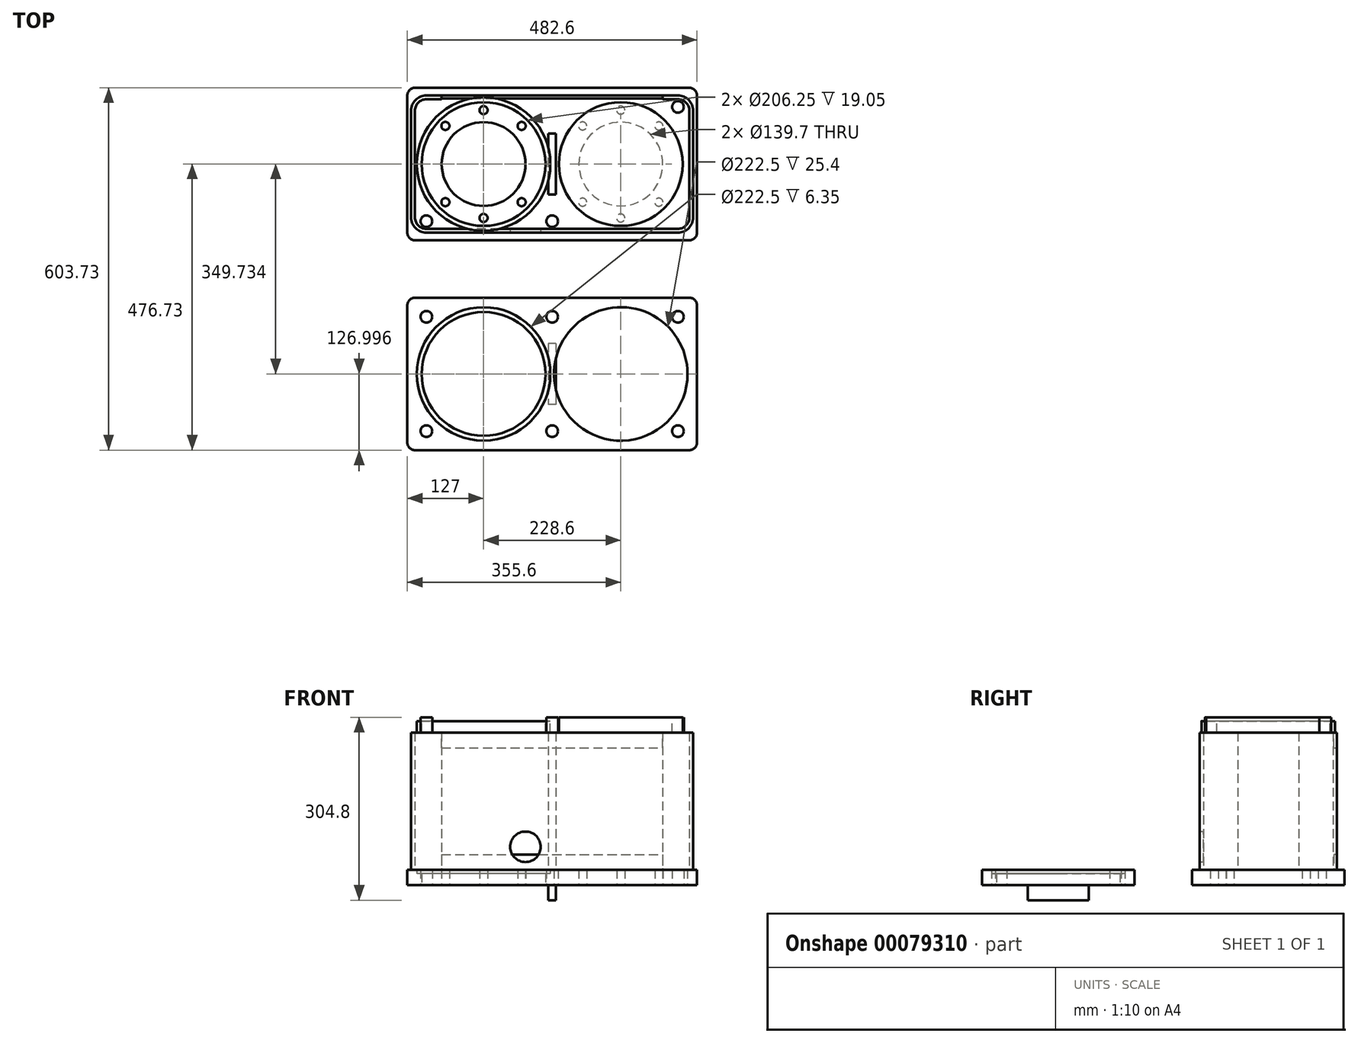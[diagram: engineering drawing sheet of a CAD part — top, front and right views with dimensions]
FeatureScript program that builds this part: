
annotation { "Feature Type Name" : "Feature", "Feature Type Description" : "" }
export const myFeature = defineFeature(function(context is Context, id is Id, definition is map)
    precondition{}
    {
        {
            var Q0;
            Q0=qCreatedBy(makeId("Top.planeOp"),FACE);
            var sketch = newSketch(context, id + "F0", { "sketchPlane" : qUnion([Q0])});
            skLineSegment(sketch, "E0.bottom", {"start": v(241.3, -127) * mm, "end": v(-241.3, -127) * mm});
            skLineSegment(sketch, "E0.top", {"start": v(241.3, 127) * mm, "end": v(-241.3, 127) * mm});
            skLineSegment(sketch, "E0.left", {"start": v(241.3, -127) * mm, "end": v(241.3, 127) * mm});
            skLineSegment(sketch, "E0.right", {"start": v(-241.3, -127) * mm, "end": v(-241.3, 127) * mm});
            skPoint(sketch, "E0.middle", {"position": v(0, 0) * mm});
            skSolve(sketch);
        }
        {
            var Q0;
            Q0=makeQuery(id+"F0.imprint","IMPRINT",FACE,{"disambiguationData":[TD([[makeQuery(id+"F0.imprint","IMPRINT",EDGE,{"derivedFrom":sQuery(id+"F0.wireOp",EDGE,"E0.bottom")}),-1.0]])]});
            extrude(context, id + "F1", {"entities" : qUnion([Q0]), "depth" : 25.4 * mm});
        }
        {
            var Q0;
            Q0=makeQuery(id+"F1.opExtrude","CAP_FACE",FACE,{"disambiguationData":[OSD([sQuery(id+"F0.wireOp",EDGE,"E0.bottom"),sQuery(id+"F0.wireOp",EDGE,"E0.top"),sQuery(id+"F0.wireOp",EDGE,"E0.left"),sQuery(id+"F0.wireOp",EDGE,"E0.right")])],"isStart":false});
            var sketch = newSketch(context, id + "F2", { "sketchPlane" : qUnion([Q0])});
            skLineSegment(sketch, "E1.bottom", {"start": v(209.55, -114.3) * mm, "end": v(-209.55, -114.3) * mm});
            skLineSegment(sketch, "E1.left", {"start": v(234.95, -88.9) * mm, "end": v(234.95, 88.9) * mm});
            skLineSegment(sketch, "E1.right", {"start": v(-234.95, -88.9) * mm, "end": v(-234.95, 88.9) * mm});
            skPoint(sketch, "E1.middle", {"position": v(0, 0) * mm});
            skLineSegment(sketch, "E2.bottom", {"start": v(209.55, -107.95) * mm, "end": v(-209.55, -107.95) * mm});
            skLineSegment(sketch, "E2.left", {"start": v(228.6, -88.9) * mm, "end": v(228.6, 88.9) * mm});
            skLineSegment(sketch, "E2.right", {"start": v(-228.6, -88.9) * mm, "end": v(-228.6, 88.9) * mm});
            skLineSegment(sketch, "E3", {"start": v(-209.55, 114.3) * mm, "end": v(-184.15, 114.3) * mm});
            skLineSegment(sketch, "E4", {"start": v(-209.55, 107.95) * mm, "end": v(-184.14, 107.95) * mm});
            skLineSegment(sketch, "E5", {"start": v(-184.15, 114.3) * mm, "end": v(-184.14, 107.95) * mm});
            skLineSegment(sketch, "E6", {"start": v(209.55, 114.3) * mm, "end": v(184.15, 114.3) * mm});
            skLineSegment(sketch, "E7", {"start": v(184.15, 114.3) * mm, "end": v(184.15, 107.95) * mm});
            skLineSegment(sketch, "E8", {"start": v(184.15, 107.95) * mm, "end": v(209.55, 107.95) * mm});
            skPoint(sketch, "E9.visualSharp", {"position": v(-234.95, 114.3) * mm});
            skArc(sketch, "E9.filletArc", {"start": v(-209.55, 114.3) * mm, "mid": v(-227.51, 106.86) * mm, "end": v(-234.95, 88.9) * mm});
            skPoint(sketch, "E10.visualSharp", {"position": v(-234.95, -114.3) * mm});
            skArc(sketch, "E10.filletArc", {"start": v(-234.95, -88.9) * mm, "mid": v(-227.51, -106.86) * mm, "end": v(-209.55, -114.3) * mm});
            skPoint(sketch, "E11.visualSharp", {"position": v(234.95, -114.3) * mm});
            skArc(sketch, "E11.filletArc", {"start": v(209.55, -114.3) * mm, "mid": v(227.51, -106.86) * mm, "end": v(234.95, -88.9) * mm});
            skPoint(sketch, "E12.visualSharp", {"position": v(234.95, 114.3) * mm});
            skArc(sketch, "E12.filletArc", {"start": v(234.95, 88.9) * mm, "mid": v(227.51, 106.86) * mm, "end": v(209.55, 114.3) * mm});
            skPoint(sketch, "E13.visualSharp", {"position": v(-228.6, 107.95) * mm});
            skArc(sketch, "E13.filletArc", {"start": v(-209.55, 107.95) * mm, "mid": v(-223.02, 102.37) * mm, "end": v(-228.6, 88.9) * mm});
            skPoint(sketch, "E14.visualSharp", {"position": v(-228.6, -107.95) * mm});
            skArc(sketch, "E14.filletArc", {"start": v(-228.6, -88.9) * mm, "mid": v(-223.02, -102.37) * mm, "end": v(-209.55, -107.95) * mm});
            skPoint(sketch, "E15.visualSharp", {"position": v(228.6, -107.95) * mm});
            skArc(sketch, "E15.filletArc", {"start": v(209.55, -107.95) * mm, "mid": v(223.02, -102.37) * mm, "end": v(228.6, -88.9) * mm});
            skPoint(sketch, "E16.visualSharp", {"position": v(228.6, 107.95) * mm});
            skArc(sketch, "E16.filletArc", {"start": v(228.6, 88.9) * mm, "mid": v(223.02, 102.37) * mm, "end": v(209.55, 107.95) * mm});
            skLineSegment(sketch, "E17.bottom", {"start": v(6.35, -50.8) * mm, "end": v(-6.35, -50.8) * mm});
            skLineSegment(sketch, "E17.top", {"start": v(6.35, 50.8) * mm, "end": v(-6.35, 50.8) * mm});
            skLineSegment(sketch, "E17.left", {"start": v(6.35, -50.8) * mm, "end": v(6.35, 50.8) * mm});
            skLineSegment(sketch, "E17.right", {"start": v(-6.35, -50.8) * mm, "end": v(-6.35, 50.8) * mm});
            skSolve(sketch);
        }
        {
            var Q0;
            Q0=makeQuery(id+"F2.imprint","IMPRINT",FACE,{"disambiguationData":[TD([[makeQuery(id+"F2.imprint","IMPRINT",EDGE,{"derivedFrom":sQuery(id+"F2.wireOp",EDGE,"E1.bottom")}),-1.0]])]});
            var Q1;
            Q1=makeQuery(id+"F2.imprint","IMPRINT",FACE,{"disambiguationData":[TD([[makeQuery(id+"F2.imprint","IMPRINT",EDGE,{"derivedFrom":sQuery(id+"F2.wireOp",EDGE,"E17.bottom")}),-1.0]])]});
            extrude(context, id + "F3", {"entities" : qUnion([Q0, Q1]), "operationType" : NewBodyOperationType.ADD, "depth" : 228.6 * mm});
        }
        {
            var Q0;
            Q0=makeQuery(id+"F3.opExtrude","CAP_FACE",FACE,{"disambiguationData":[OSD([sQuery(id+"F2.wireOp",EDGE,"E1.bottom"),sQuery(id+"F2.wireOp",EDGE,"E1.left"),sQuery(id+"F2.wireOp",EDGE,"E1.right"),sQuery(id+"F2.wireOp",EDGE,"E2.bottom"),sQuery(id+"F2.wireOp",EDGE,"E2.left"),sQuery(id+"F2.wireOp",EDGE,"E2.right"),sQuery(id+"F2.wireOp",EDGE,"E3"),sQuery(id+"F2.wireOp",EDGE,"E4"),sQuery(id+"F2.wireOp",EDGE,"E5"),sQuery(id+"F2.wireOp",EDGE,"E6"),sQuery(id+"F2.wireOp",EDGE,"E7"),sQuery(id+"F2.wireOp",EDGE,"E8"),sQuery(id+"F2.wireOp",EDGE,"E9.filletArc"),sQuery(id+"F2.wireOp",EDGE,"E10.filletArc"),sQuery(id+"F2.wireOp",EDGE,"E11.filletArc"),sQuery(id+"F2.wireOp",EDGE,"E12.filletArc"),sQuery(id+"F2.wireOp",EDGE,"E13.filletArc"),sQuery(id+"F2.wireOp",EDGE,"E14.filletArc"),sQuery(id+"F2.wireOp",EDGE,"E15.filletArc"),sQuery(id+"F2.wireOp",EDGE,"E16.filletArc")])],"isStart":false});
            var sketch = newSketch(context, id + "F4", { "sketchPlane" : qUnion([Q0])});
            skLineSegment(sketch, "E18.bottom", {"start": v(241.3, -127) * mm, "end": v(-241.3, -127) * mm});
            skLineSegment(sketch, "E18.top", {"start": v(241.3, 127) * mm, "end": v(-241.3, 127) * mm});
            skLineSegment(sketch, "E18.left", {"start": v(241.3, -127) * mm, "end": v(241.3, 127) * mm});
            skLineSegment(sketch, "E18.right", {"start": v(-241.3, -127) * mm, "end": v(-241.3, 127) * mm});
            skPoint(sketch, "E18.middle", {"position": v(0, 0) * mm});
            skSolve(sketch);
        }
        {
            var Q0;
            Q0 = qSketchRegion(id + "F4", true);
            extrude(context, id + "F5", {"entities" : qUnion([Q0]), "operationType" : NewBodyOperationType.ADD, "depth" : 25.4 * mm});
        }
        {
            var Q0;
            Q0=makeQuery(id+"F3.opExtrude","SWEPT_FACE",FACE,{"disambiguationData":[OSD([sQuery(id+"F2.wireOp",EDGE,"E1.bottom")])]});
            var sketch = newSketch(context, id + "F6", { "sketchPlane" : qUnion([Q0])});
            skCircle(sketch, "E19", {"center": v(-44.45, 63.5) * mm, "radius": 25.4 * mm});
            skSolve(sketch);
        }
        {
            var Q0;
            Q0=makeQuery(id+"F6.imprint","IMPRINT",FACE,{"disambiguationData":[TD([[makeQuery(id+"F6.imprint","IMPRINT",EDGE,{"derivedFrom":sQuery(id+"F6.wireOp",EDGE,"E19")}),1.0]])]});
            extrude(context, id + "F7", {"entities" : qUnion([Q0]), "operationType" : NewBodyOperationType.REMOVE, "oppositeDirection" : true, "depth" : 6.35 * mm});
        }
        {
            var Q0;
            Q0=qCreatedBy(makeId("Right.planeOp"),FACE);
            var sketch = newSketch(context, id + "F8", { "sketchPlane" : qUnion([Q0])});
            skLineSegment(sketch, "E20", {"start": v(0, -47.78) * mm, "end": v(0, 307.42) * mm, "construction": true});
            skSolve(sketch);
        }
        {
            var Q0;
            Q0=makeQuery(id+"F5.opExtrude","CAP_FACE",FACE,{"disambiguationData":[OSD([sQuery(id+"F4.wireOp",EDGE,"E18.bottom"),sQuery(id+"F4.wireOp",EDGE,"E18.top"),sQuery(id+"F4.wireOp",EDGE,"E18.left"),sQuery(id+"F4.wireOp",EDGE,"E18.right")])],"isStart":false});
            var sketch = newSketch(context, id + "F9", { "sketchPlane" : qUnion([Q0])});
            skLineSegment(sketch, "E21", {"start": v(-287.61, 0) * mm, "end": v(290.97, 0) * mm, "construction": true});
            skPoint(sketch, "E21.endSnap0", {"position": v(-241.3, 0) * mm});
            skCircle(sketch, "E22", {"center": v(-114.3, 0) * mm, "radius": 111.25 * mm});
            skCircle(sketch, "E23", {"center": v(-114.3, 0) * mm, "radius": 103.12 * mm});
            skLineSegment(sketch, "E24", {"start": v(0, 159.16) * mm, "end": v(0, -163.18) * mm, "construction": true});
            skCircle(sketch, "E25.MirrorC", {"center": v(114.3, 0) * mm, "radius": 111.25 * mm});
            skCircle(sketch, "E26.MirrorC", {"center": v(114.3, 0) * mm, "radius": 103.12 * mm});
            skCircle(sketch, "E27", {"center": v(-209.55, 95.25) * mm, "radius": 9.72 * mm});
            skCircle(sketch, "E28", {"center": v(0, 95.25) * mm, "radius": 9.72 * mm});
            skCircle(sketch, "E29.MirrorC", {"center": v(209.55, 95.25) * mm, "radius": 9.72 * mm});
            skCircle(sketch, "E30.MirrorC", {"center": v(-209.55, -95.25) * mm, "radius": 9.72 * mm});
            skCircle(sketch, "E31.MirrorC", {"center": v(0, -95.25) * mm, "radius": 9.72 * mm});
            skCircle(sketch, "E32.MirrorC", {"center": v(209.55, -95.25) * mm, "radius": 9.72 * mm});
            skSolve(sketch);
        }
        {
            var Q0;
            Q0=makeQuery(id+"F9.imprint","IMPRINT",FACE,{"disambiguationData":[TD([[makeQuery(id+"F9.imprint","IMPRINT",EDGE,{"derivedFrom":sQuery(id+"F9.wireOp",EDGE,"E23")}),1.0]])]});
            var Q1;
            Q1=makeQuery(id+"F9.imprint","IMPRINT",FACE,{"disambiguationData":[TD([[makeQuery(id+"F9.imprint","IMPRINT",EDGE,{"derivedFrom":sQuery(id+"F9.wireOp",EDGE,"E26.MirrorC")}),-1.0]])]});
            extrude(context, id + "F10", {"entities" : qUnion([Q0, Q1]), "operationType" : NewBodyOperationType.REMOVE, "oppositeDirection" : true, "depth" : 25.4 * mm});
        }
        {
            var Q0;
            Q0=makeQuery(id+"F9.imprint","IMPRINT",FACE,{"disambiguationData":[TD([[makeQuery(id+"F9.imprint","IMPRINT",EDGE,{"derivedFrom":sQuery(id+"F9.wireOp",EDGE,"E22")}),1.0]])]});
            var Q1;
            Q1=makeQuery(id+"F9.imprint","IMPRINT",FACE,{"disambiguationData":[TD([[makeQuery(id+"F9.imprint","IMPRINT",EDGE,{"derivedFrom":sQuery(id+"F9.wireOp",EDGE,"E25.MirrorC")}),-1.0]])]});
            extrude(context, id + "F11", {"entities" : qUnion([Q0, Q1]), "operationType" : NewBodyOperationType.REMOVE, "oppositeDirection" : true, "depth" : 6.35 * mm});
        }
        {
            var Q0;
            Q0=makeQuery(id+"F9.imprint","IMPRINT",FACE,{"disambiguationData":[TD([[makeQuery(id+"F9.imprint","IMPRINT",EDGE,{"derivedFrom":sQuery(id+"F9.wireOp",EDGE,"E27")}),1.0]])]});
            var Q1;
            Q1=makeQuery(id+"F9.imprint","IMPRINT",FACE,{"disambiguationData":[TD([[makeQuery(id+"F9.imprint","IMPRINT",EDGE,{"derivedFrom":sQuery(id+"F9.wireOp",EDGE,"E28")}),1.0]])]});
            var Q2;
            Q2=makeQuery(id+"F9.imprint","IMPRINT",FACE,{"disambiguationData":[TD([[makeQuery(id+"F9.imprint","IMPRINT",EDGE,{"derivedFrom":sQuery(id+"F9.wireOp",EDGE,"E29.MirrorC")}),-1.0]])]});
            var Q3;
            Q3=makeQuery(id+"F9.imprint","IMPRINT",FACE,{"disambiguationData":[TD([[makeQuery(id+"F9.imprint","IMPRINT",EDGE,{"derivedFrom":sQuery(id+"F9.wireOp",EDGE,"E32.MirrorC")}),1.0]])]});
            var Q4;
            Q4=makeQuery(id+"F9.imprint","IMPRINT",FACE,{"disambiguationData":[TD([[makeQuery(id+"F9.imprint","IMPRINT",EDGE,{"derivedFrom":sQuery(id+"F9.wireOp",EDGE,"E31.MirrorC")}),-1.0]])]});
            var Q5;
            Q5=makeQuery(id+"F9.imprint","IMPRINT",FACE,{"disambiguationData":[TD([[makeQuery(id+"F9.imprint","IMPRINT",EDGE,{"derivedFrom":sQuery(id+"F9.wireOp",EDGE,"E30.MirrorC")}),-1.0]])]});
            extrude(context, id + "F12", {"entities" : qUnion([Q0, Q1, Q2, Q3, Q4, Q5]), "operationType" : NewBodyOperationType.REMOVE, "oppositeDirection" : true, "depth" : 25.4 * mm});
        }
        {
            var Q0;
            Q0=makeQuery(id+"F1.opExtrude","CAP_FACE",FACE,{"disambiguationData":[OSD([sQuery(id+"F0.wireOp",EDGE,"E0.bottom"),sQuery(id+"F0.wireOp",EDGE,"E0.top"),sQuery(id+"F0.wireOp",EDGE,"E0.left"),sQuery(id+"F0.wireOp",EDGE,"E0.right")])],"isStart":true});
            var sketch = newSketch(context, id + "F13", { "sketchPlane" : qUnion([Q0])});
            skCircle(sketch, "E33", {"center": v(114.3, 0) * mm, "radius": 69.85 * mm});
            skLineSegment(sketch, "E34", {"start": v(285.43, 0) * mm, "end": v(-294.1, 0) * mm, "construction": true});
            skPoint(sketch, "E34.endSnap0", {"position": v(-241.3, 0) * mm});
            skLineSegment(sketch, "E35", {"start": v(0, -149.02) * mm, "end": v(0, 174.43) * mm, "construction": true});
            skCircle(sketch, "E36", {"center": v(114.3, -89.81) * mm, "radius": 6.75 * mm});
            skLineSegment(sketch, "E37", {"start": v(114.3, 0) * mm, "end": v(177.8, -63.5) * mm, "construction": true});
            skCircle(sketch, "E38", {"center": v(177.8, -63.5) * mm, "radius": 6.75 * mm});
            skLineSegment(sketch, "E39", {"start": v(114.3, 0) * mm, "end": v(50.8, -63.5) * mm, "construction": true});
            skCircle(sketch, "E40", {"center": v(50.8, -63.5) * mm, "radius": 6.75 * mm});
            skCircle(sketch, "E41.MirrorC", {"center": v(50.8, 63.5) * mm, "radius": 6.75 * mm});
            skCircle(sketch, "E42.MirrorC", {"center": v(114.3, 89.81) * mm, "radius": 6.75 * mm});
            skCircle(sketch, "E43.MirrorC", {"center": v(177.8, 63.5) * mm, "radius": 6.75 * mm});
            skCircle(sketch, "E44.MirrorC", {"center": v(-50.8, -63.5) * mm, "radius": 6.75 * mm});
            skCircle(sketch, "E45.MirrorC", {"center": v(-114.3, -89.81) * mm, "radius": 6.75 * mm});
            skCircle(sketch, "E46.MirrorC", {"center": v(-177.8, -63.5) * mm, "radius": 6.75 * mm});
            skCircle(sketch, "E47.MirrorC", {"center": v(-114.3, 0) * mm, "radius": 69.85 * mm});
            skCircle(sketch, "E48.MirrorC", {"center": v(-50.8, 63.5) * mm, "radius": 6.75 * mm});
            skCircle(sketch, "E49.MirrorC", {"center": v(-114.3, 89.81) * mm, "radius": 6.75 * mm});
            skCircle(sketch, "E50.MirrorC", {"center": v(-177.8, 63.5) * mm, "radius": 6.75 * mm});
            skSolve(sketch);
        }
        {
            var Q0;
            Q0 = qSketchRegion(id + "F13", true);
            extrude(context, id + "F14", {"entities" : qUnion([Q0]), "operationType" : NewBodyOperationType.REMOVE, "oppositeDirection" : true, "depth" : 25.4 * mm});
        }
        {
            var Q0;
            Q0=makeQuery(id+"F1.opExtrude","CAP_FACE",FACE,{"disambiguationData":[OSD([sQuery(id+"F0.wireOp",EDGE,"E0.bottom"),sQuery(id+"F0.wireOp",EDGE,"E0.top"),sQuery(id+"F0.wireOp",EDGE,"E0.left"),sQuery(id+"F0.wireOp",EDGE,"E0.right")])],"isStart":false});
            var sketch = newSketch(context, id + "F15", { "sketchPlane" : qUnion([Q0])});
            skLineSegment(sketch, "E51.bottom", {"start": v(-184.15, 114.3) * mm, "end": v(184.15, 114.3) * mm});
            skLineSegment(sketch, "E51.top", {"start": v(-184.15, 109.54) * mm, "end": v(184.15, 109.54) * mm});
            skLineSegment(sketch, "E51.left", {"start": v(-184.15, 114.3) * mm, "end": v(-184.15, 109.54) * mm});
            skLineSegment(sketch, "E51.right", {"start": v(184.15, 114.3) * mm, "end": v(184.15, 109.54) * mm});
            skSolve(sketch);
        }
        {
            var Q0;
            {var subQ0=sQuery(id+"F15.wireOp",EDGE,"E51.bottom");Q0=makeQuery(id+"F15.imprint","IMPRINT",FACE,{"disambiguationData":[TD([[makeQuery(id+"F15.imprint","IMPRINT",EDGE,{"derivedFrom":subQ0}),-1.0]])]});}
            extrude(context, id + "F16", {"entities" : qUnion([Q0]), "depth" : 25.4 * mm});
        }
        {
            var Q0;
            Q0=makeQuery(id+"F5.opExtrude","CAP_FACE",FACE,{"disambiguationData":[OSD([sQuery(id+"F4.wireOp",EDGE,"E18.bottom"),sQuery(id+"F4.wireOp",EDGE,"E18.top"),sQuery(id+"F4.wireOp",EDGE,"E18.left"),sQuery(id+"F4.wireOp",EDGE,"E18.right")])],"isStart":true});
            var sketch = newSketch(context, id + "F17", { "sketchPlane" : qUnion([Q0])});
            skLineSegment(sketch, "E52.bottom", {"start": v(-184.15, -109.54) * mm, "end": v(184.15, -109.54) * mm});
            skLineSegment(sketch, "E52.top", {"start": v(-184.15, -114.3) * mm, "end": v(184.15, -114.3) * mm});
            skLineSegment(sketch, "E52.left", {"start": v(-184.15, -109.54) * mm, "end": v(-184.15, -114.3) * mm});
            skLineSegment(sketch, "E52.right", {"start": v(184.15, -109.54) * mm, "end": v(184.15, -114.3) * mm});
            skPoint(sketch, "E52.middle", {"position": v(0, -111.92) * mm});
            skSolve(sketch);
        }
        {
            var Q0;
            {var subQ4=sQuery(id+"F17.wireOp",EDGE,"E52.top");Q0=makeQuery(id+"F17.imprint","IMPRINT",FACE,{"disambiguationData":[TD([[makeQuery(id+"F17.imprint","IMPRINT",EDGE,{"derivedFrom":subQ4}),1.0]])]});}
            extrude(context, id + "F18", {"entities" : qUnion([Q0]), "depth" : 25.4 * mm});
        }
        {
            var Q0;
            Q0=qCreatedBy(makeId("Top.planeOp"),FACE);
            var sketch = newSketch(context, id + "F19", { "sketchPlane" : qUnion([Q0])});
            skLineSegment(sketch, "E53.bottom", {"start": v(241.3, -222.73) * mm, "end": v(-241.3, -222.73) * mm});
            skLineSegment(sketch, "E53.top", {"start": v(241.3, -476.73) * mm, "end": v(-241.3, -476.73) * mm});
            skLineSegment(sketch, "E53.left", {"start": v(241.3, -222.73) * mm, "end": v(241.3, -476.73) * mm});
            skLineSegment(sketch, "E53.right", {"start": v(-241.3, -222.73) * mm, "end": v(-241.3, -476.73) * mm});
            skPoint(sketch, "E53.middle", {"position": v(0, -349.73) * mm});
            skLineSegment(sketch, "E54", {"start": v(-287.61, -349.73) * mm, "end": v(-209.17, -349.73) * mm, "construction": true});
            skPoint(sketch, "E54.endSnap0", {"position": v(-241.3, -349.73) * mm});
            skCircle(sketch, "E55", {"center": v(-114.3, -349.73) * mm, "radius": 111.25 * mm});
            skCircle(sketch, "E56", {"center": v(-114.3, -349.73) * mm, "radius": 103.12 * mm});
            skLineSegment(sketch, "E57", {"start": v(0, -190.83) * mm, "end": v(0, -513.17) * mm, "construction": true});
            skCircle(sketch, "E58.MirrorC", {"center": v(114.3, -349.73) * mm, "radius": 111.25 * mm});
            skCircle(sketch, "E59.MirrorC", {"center": v(114.3, -349.73) * mm, "radius": 103.12 * mm});
            skCircle(sketch, "E60", {"center": v(-209.55, -254.48) * mm, "radius": 9.72 * mm});
            skCircle(sketch, "E61", {"center": v(0, -254.48) * mm, "radius": 9.72 * mm});
            skCircle(sketch, "E62.MirrorC", {"center": v(209.55, -254.48) * mm, "radius": 9.72 * mm});
            skCircle(sketch, "E63.MirrorC", {"center": v(-209.55, -444.98) * mm, "radius": 9.72 * mm});
            skCircle(sketch, "E64.MirrorC", {"center": v(0, -444.98) * mm, "radius": 9.72 * mm});
            skCircle(sketch, "E65.MirrorC", {"center": v(209.55, -444.98) * mm, "radius": 9.72 * mm});
            skSolve(sketch);
        }
        {
            var Q0;
            Q0=makeQuery(id+"F19.imprint","IMPRINT",FACE,{"disambiguationData":[TD([[makeQuery(id+"F19.imprint","IMPRINT",EDGE,{"derivedFrom":sQuery(id+"F19.wireOp",EDGE,"E53.bottom")}),1.0]])]});
            extrude(context, id + "F20", {"entities" : qUnion([Q0]), "depth" : 25.4 * mm});
        }
        {
            var Q0;
            Q0=makeQuery(id+"F19.imprint","IMPRINT",FACE,{"disambiguationData":[TD([[makeQuery(id+"F19.imprint","IMPRINT",EDGE,{"derivedFrom":sQuery(id+"F19.wireOp",EDGE,"E55")}),1.0]])]});
            var Q1;
            Q1=makeQuery(id+"F19.imprint","IMPRINT",FACE,{"disambiguationData":[TD([[makeQuery(id+"F19.imprint","IMPRINT",EDGE,{"derivedFrom":sQuery(id+"F19.wireOp",EDGE,"E58.MirrorC")}),-1.0]])]});
            extrude(context, id + "F21", {"entities" : qUnion([Q0, Q1]), "operationType" : NewBodyOperationType.ADD, "depth" : 19.05 * mm});
        }
        {
            var Q0;
            {var subQ0=sQuery(id+"F19.wireOp",EDGE,"E58.MirrorC");var subQ1=sQuery(id+"F19.wireOp",EDGE,"E55");Q0=makeQuery(id+"F21.boolean.opBoolean","MERGE",FACE,{"derivedFrom":[makeQuery(id+"F20.opExtrude","CAP_FACE",FACE,{"disambiguationData":[OSD([sQuery(id+"F19.wireOp",EDGE,"E53.bottom"),sQuery(id+"F19.wireOp",EDGE,"E53.top"),sQuery(id+"F19.wireOp",EDGE,"E53.left"),sQuery(id+"F19.wireOp",EDGE,"E53.right"),subQ1,subQ0,sQuery(id+"F19.wireOp",EDGE,"E60"),sQuery(id+"F19.wireOp",EDGE,"E61"),sQuery(id+"F19.wireOp",EDGE,"E62.MirrorC"),sQuery(id+"F19.wireOp",EDGE,"E63.MirrorC"),sQuery(id+"F19.wireOp",EDGE,"E64.MirrorC"),sQuery(id+"F19.wireOp",EDGE,"E65.MirrorC")])],"isStart":true}),makeQuery(id+"F21.opExtrude","CAP_FACE",FACE,{"disambiguationData":[OSD([subQ1,sQuery(id+"F19.wireOp",EDGE,"E56")])],"isStart":true}),makeQuery(id+"F21.opExtrude","CAP_FACE",FACE,{"disambiguationData":[OSD([subQ0,sQuery(id+"F19.wireOp",EDGE,"E59.MirrorC")])],"isStart":true})]});}
            var sketch = newSketch(context, id + "F22", { "sketchPlane" : qUnion([Q0])});
            skLineSegment(sketch, "E66.bottom", {"start": v(6.35, 298.93) * mm, "end": v(-6.35, 298.93) * mm});
            skLineSegment(sketch, "E66.top", {"start": v(6.35, 400.53) * mm, "end": v(-6.35, 400.53) * mm});
            skLineSegment(sketch, "E66.left", {"start": v(6.35, 298.93) * mm, "end": v(6.35, 400.53) * mm});
            skLineSegment(sketch, "E66.right", {"start": v(-6.35, 298.93) * mm, "end": v(-6.35, 400.53) * mm});
            skPoint(sketch, "E66.middle", {"position": v(0, 349.73) * mm});
            skSolve(sketch);
        }
        {
            var Q0;
            Q0 = qSketchRegion(id + "F22", true);
            extrude(context, id + "F23", {"entities" : qUnion([Q0]), "operationType" : NewBodyOperationType.ADD, "depth" : 25.4 * mm});
        }
        {
            var Q0;
            Q0=makeQuery(id+"F5.opExtrude","SWEPT_EDGE",EDGE,{"disambiguationData":[OSD([sQuery(id+"F4.wireOp",EDGE,"E18.bottom"),sQuery(id+"F4.wireOp",EDGE,"E18.left")])]});
            var Q1;
            Q1=makeQuery(id+"F5.opExtrude","SWEPT_EDGE",EDGE,{"disambiguationData":[OSD([sQuery(id+"F4.wireOp",EDGE,"E18.top"),sQuery(id+"F4.wireOp",EDGE,"E18.left")])]});
            var Q2;
            Q2=makeQuery(id+"F1.opExtrude","SWEPT_EDGE",EDGE,{"disambiguationData":[OSD([sQuery(id+"F0.wireOp",EDGE,"E0.top"),sQuery(id+"F0.wireOp",EDGE,"E0.left")])]});
            var Q3;
            Q3=makeQuery(id+"F1.opExtrude","SWEPT_EDGE",EDGE,{"disambiguationData":[OSD([sQuery(id+"F0.wireOp",EDGE,"E0.bottom"),sQuery(id+"F0.wireOp",EDGE,"E0.left")])]});
            var Q4;
            Q4=makeQuery(id+"F5.opExtrude","SWEPT_EDGE",EDGE,{"disambiguationData":[OSD([sQuery(id+"F4.wireOp",EDGE,"E18.bottom"),sQuery(id+"F4.wireOp",EDGE,"E18.right")])]});
            var Q5;
            Q5=makeQuery(id+"F5.opExtrude","SWEPT_EDGE",EDGE,{"disambiguationData":[OSD([sQuery(id+"F4.wireOp",EDGE,"E18.top"),sQuery(id+"F4.wireOp",EDGE,"E18.right")])]});
            var Q6;
            Q6=makeQuery(id+"F1.opExtrude","SWEPT_EDGE",EDGE,{"disambiguationData":[OSD([sQuery(id+"F0.wireOp",EDGE,"E0.top"),sQuery(id+"F0.wireOp",EDGE,"E0.right")])]});
            var Q7;
            Q7=makeQuery(id+"F1.opExtrude","SWEPT_EDGE",EDGE,{"disambiguationData":[OSD([sQuery(id+"F0.wireOp",EDGE,"E0.bottom"),sQuery(id+"F0.wireOp",EDGE,"E0.right")])]});
            var Q8;
            Q8=makeQuery(id+"F20.opExtrude","SWEPT_EDGE",EDGE,{"disambiguationData":[OSD([sQuery(id+"F19.wireOp",EDGE,"E53.top"),sQuery(id+"F19.wireOp",EDGE,"E53.right")])]});
            var Q9;
            Q9=makeQuery(id+"F20.opExtrude","SWEPT_EDGE",EDGE,{"disambiguationData":[OSD([sQuery(id+"F19.wireOp",EDGE,"E53.bottom"),sQuery(id+"F19.wireOp",EDGE,"E53.right")])]});
            var Q10;
            Q10=makeQuery(id+"F20.opExtrude","SWEPT_EDGE",EDGE,{"disambiguationData":[OSD([sQuery(id+"F19.wireOp",EDGE,"E53.bottom"),sQuery(id+"F19.wireOp",EDGE,"E53.left")])]});
            var Q11;
            Q11=makeQuery(id+"F20.opExtrude","SWEPT_EDGE",EDGE,{"disambiguationData":[OSD([sQuery(id+"F19.wireOp",EDGE,"E53.top"),sQuery(id+"F19.wireOp",EDGE,"E53.left")])]});
            fillet(context, id + "F24", {"entities" : qUnion([Q0, Q1, Q2, Q3, Q4, Q5, Q6, Q7, Q8, Q9, Q10, Q11]), "radius" : 12.7 * mm, "tangentPropagation" : true, "allowEdgeOverflow" : false});
        }
    });
